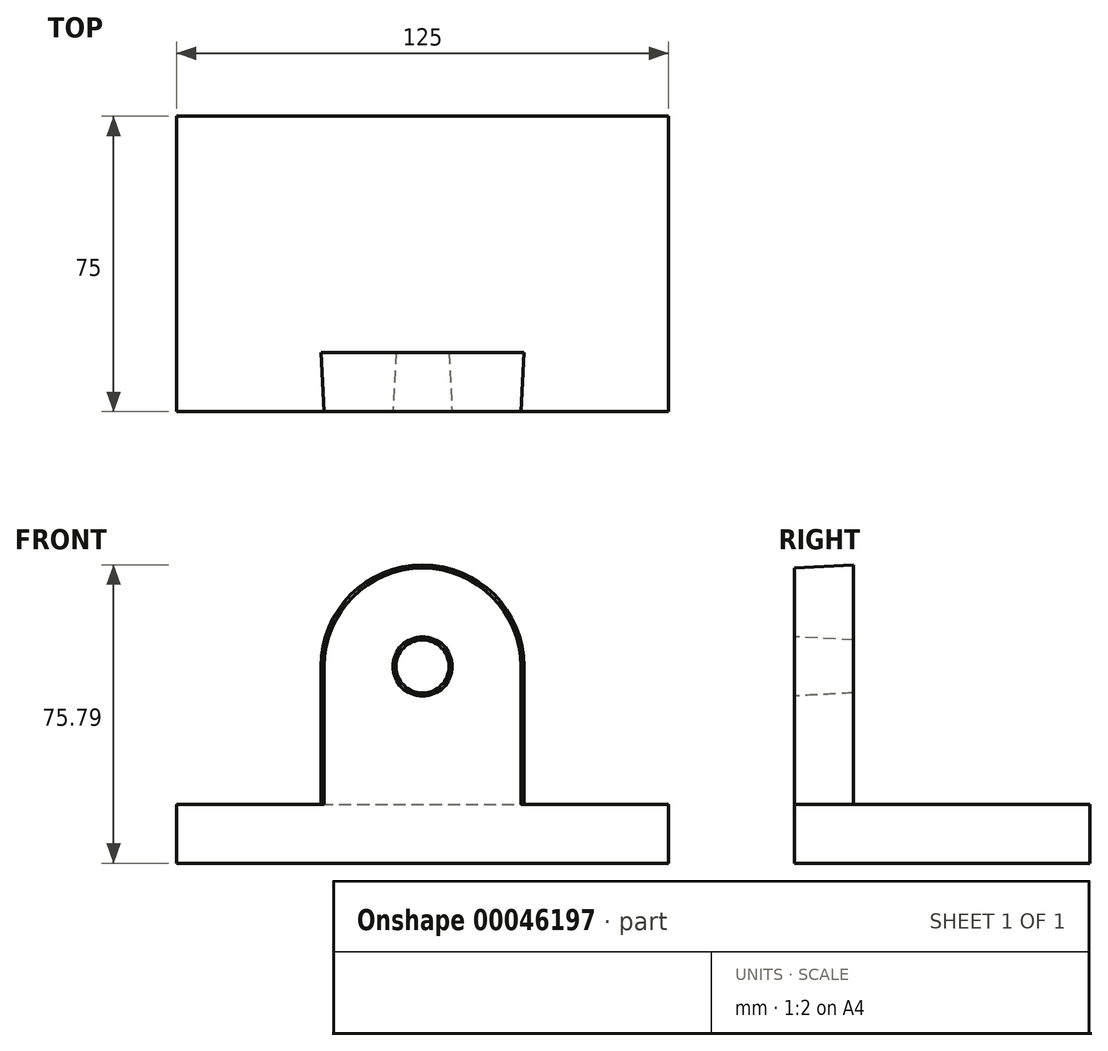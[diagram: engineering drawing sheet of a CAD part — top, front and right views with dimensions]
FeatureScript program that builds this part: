
annotation { "Feature Type Name" : "Feature", "Feature Type Description" : "" }
export const myFeature = defineFeature(function(context is Context, id is Id, definition is map)
    precondition{}
    {
        {
            var Q0;
            Q0=qCreatedBy(makeId("Top.planeOp"),FACE);
            var sketch = newSketch(context, id + "F0", { "sketchPlane" : qUnion([Q0])});
            skLineSegment(sketch, "E0.rect.bottom", {"start": v(-62.5, 37.5) * mm, "end": v(62.5, 37.5) * mm});
            skLineSegment(sketch, "E0.rect.top", {"start": v(-62.5, -37.5) * mm, "end": v(62.5, -37.5) * mm});
            skLineSegment(sketch, "E0.rect.left", {"start": v(-62.5, 37.5) * mm, "end": v(-62.5, -37.5) * mm});
            skLineSegment(sketch, "E0.rect.right", {"start": v(62.5, 37.5) * mm, "end": v(62.5, -37.5) * mm});
            skPoint(sketch, "E0.rect.middle", {"position": v(0, 0) * mm});
            skSolve(sketch);
        }
        {
            var Q0;
            Q0=makeQuery(id+"F0.imprint","IMPRINT",FACE,{"disambiguationData":[TD([[makeQuery(id+"F0.imprint","IMPRINT",EDGE,{"derivedFrom":sQuery(id+"F0.wireOp",EDGE,"E0.rect.bottom")}),-1.0]])]});
            extrude(context, id + "F1", {"entities" : qUnion([Q0]), "depth" : 15 * mm});
        }
        {
            var Q0;
            Q0=makeQuery(id+"F1.opExtrude","SWEPT_FACE",FACE,{"disambiguationData":[OSD([sQuery(id+"F0.wireOp",EDGE,"E0.rect.top")])]});
            var sketch = newSketch(context, id + "F2", { "sketchPlane" : qUnion([Q0])});
            skLineSegment(sketch, "E1", {"start": v(0, 0) * mm, "end": v(0, 50) * mm, "construction": true});
            skCircle(sketch, "E2", {"center": v(0, 50) * mm, "radius": 25 * mm});
            skLineSegment(sketch, "E3.bottom", {"start": v(-25, 50) * mm, "end": v(25, 50) * mm});
            skLineSegment(sketch, "E3.top", {"start": v(-25, 0) * mm, "end": v(25, 0) * mm});
            skLineSegment(sketch, "E3.left", {"start": v(-25, 50) * mm, "end": v(-25, 0) * mm});
            skLineSegment(sketch, "E3.right", {"start": v(25, 50) * mm, "end": v(25, 0) * mm});
            skCircle(sketch, "E4", {"center": v(0, 50) * mm, "radius": 7.5 * mm});
            skSolve(sketch);
        }
        {
            var Q0;
            {var subQ0=sQuery(id+"F2.wireOp",EDGE,"E3.bottom");Q0=makeQuery(id+"F2.imprint","IMPRINT",FACE,{"disambiguationData":[TD([[makeQuery(id+"F2.imprint","IMPRINT",EDGE,{"derivedFrom":subQ0}),1.0]])]});}
            var Q1;
            {var subQ0=sQuery(id+"F2.wireOp",EDGE,"E3.bottom");Q1=makeQuery(id+"F2.imprint","IMPRINT",FACE,{"disambiguationData":[TD([[makeQuery(id+"F2.imprint","IMPRINT",EDGE,{"derivedFrom":subQ0}),-1.0]])]});}
            var Q2;
            {var subQ0=makeQuery(id+"F1.opExtrude","CAP_EDGE",EDGE,{"disambiguationData":[OSD([sQuery(id+"F0.wireOp",EDGE,"E0.rect.top")])],"isStart":false});var subQ3=sQuery(id+"F2.wireOp",EDGE,"E3.left");var subQ4=makeQuery(id+"F2.imprint","INTERSECT",VERTEX,{"derivedFrom":[subQ0,subQ3]});Q2=makeQuery(id+"F2.imprint","IMPRINT",FACE,{"disambiguationData":[TD([[makeQuery(id+"F2.imprint","IMPRINT",EDGE,{"disambiguationData":[TD([[subQ4,-1.0]])],"derivedFrom":subQ0}),1.0]])]});}
            extrude(context, id + "F3", {"entities" : qUnion([Q0, Q1, Q2]), "operationType" : NewBodyOperationType.ADD, "oppositeDirection" : true, "depth" : 15 * mm, "hasDraft" : true, "draftAngle" : 3 * degree});
        }
    });
